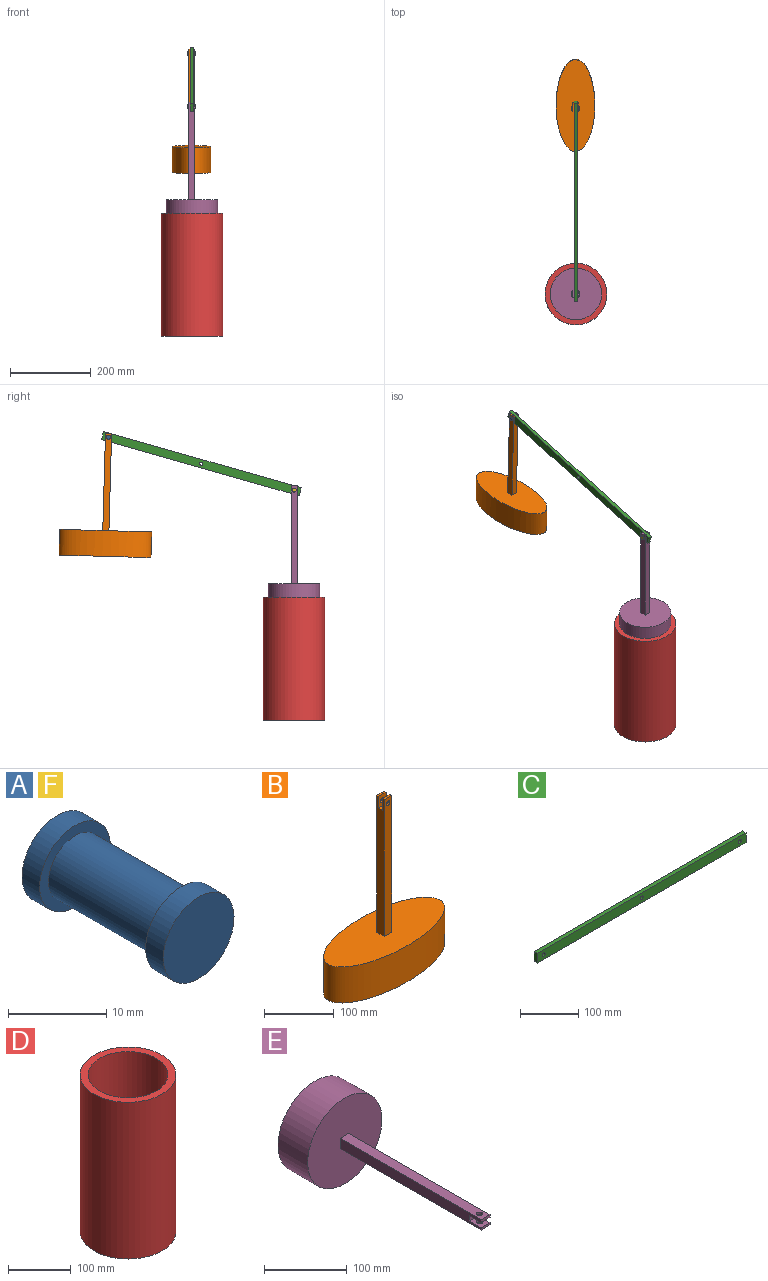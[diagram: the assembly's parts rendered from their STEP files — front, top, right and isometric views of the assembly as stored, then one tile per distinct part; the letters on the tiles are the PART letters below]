
ASSEMBLY  parts=6 mates=5
PART A: 7 faces, bbox 10.2x20.3x10.2 mm
  f0: cylinder r=3.81mm len=15.24mm, axis (0,1,0), area 364.8mm2, adj f3,f6
  f1: cylinder r=5.08mm len=10.16mm, axis (0,1,0), area 81.1mm2, adj f2,f3
  f2: plane 10.16x10.16mm, normal (0,-1,0), area 81.1mm2, adj f1
  f3: plane 10.16x10.16mm, normal (0,1,0), area 35.5mm2, adj f0,f1
  f4: cylinder r=5.08mm len=10.16mm, axis (0,-1,0), area 81.1mm2, adj f5,f6
  f5: plane 10.16x10.16mm, normal (0,1,0), area 81.1mm2, adj f4
  f6: plane 10.16x10.16mm, normal (0,-1,0), area 35.5mm2, adj f0,f4
PART B: 14 faces, bbox 226.9x95.8x304.8 mm
  f0: plane 15.24x3.8mm, normal (0,0,1), area 57.9mm2, adj f4,f5,f7,f10
  f1: plane 226.88x95.83mm, normal (0,0,1), area 16843.5mm2, adj f2,f4,f5,f6,f7
  f2: extruded ~226.88x95.83mm, area 33533.4mm2, adj f1,f3
  f3: plane 226.88x95.83mm, normal (0,0,-1), area 17075.7mm2, adj f2
  f4: plane 241.3x15.24mm, normal (0,1,0), area 3631.8mm2, adj f0,f1,f5,f7,f12
  f5: plane 241.3x15.24mm, normal (-1,0,0), area 3513.6mm2, adj f0,f1,f4,f6,f8,f9,f10,f11
  f6: plane 241.3x15.24mm, normal (0,-1,0), area 3631.8mm2, adj f1,f5,f7,f8,f13
  f7: plane 241.3x15.24mm, normal (1,0,0), area 3513.6mm2, adj f0,f1,f4,f6,f8,f9,f10,f11
  f8: plane 15.24x3.38mm, normal (0,0,1), area 51.5mm2, adj f5,f6,f7,f9
  f9: plane 20.32x15.24mm, normal (0,1,0), area 264.1mm2, adj f5,f7,f8,f11,f13
  f10: plane 20.32x15.24mm, normal (0,-1,0), area 264.1mm2, adj f0,f5,f7,f11,f12
  f11: plane 15.24x8.06mm, normal (0,0,1), area 122.8mm2, adj f5,f7,f9,f10
  f12: cylinder r=3.81mm len=7.62mm, axis (0,-1,0), area 90.9mm2, adj f4,f10
  f13: cylinder r=3.81mm len=7.62mm, axis (0,1,0), area 81mm2, adj f6,f9
PART C: 9 faces, bbox 508x8.1x20.3 mm
  f0: plane 20.32x8.05mm, normal (1,0,0), area 163.6mm2, adj f1,f3,f4,f5
  f1: plane 508x8.05mm, normal (0,0,1), area 4090.3mm2, adj f0,f2,f4,f5
  f2: plane 20.32x8.05mm, normal (-1,0,0), area 163.6mm2, adj f1,f3,f4,f5
  f3: plane 508x8.05mm, normal (0,0,-1), area 4090.3mm2, adj f0,f2,f4,f5
  f4: plane 508x20.32mm, normal (0,-1,0), area 10185.7mm2, adj f0,f1,f2,f3,f6,f7,f8
  f5: plane 508x20.32mm, normal (0,1,0), area 10185.7mm2, adj f0,f1,f2,f3,f6,f7,f8
  f6: cylinder r=3.81mm len=8.05mm, axis (0,-1,0), area 192.8mm2, adj f4,f5
  f7: cylinder r=3.81mm len=8.05mm, axis (0,-1,0), area 192.8mm2, adj f4,f5
  f8: cylinder r=3.81mm len=8.05mm, axis (0,-1,0), area 192.8mm2, adj f4,f5
PART D: 4 faces, bbox 152.4x152.4x304.8 mm
  f0: cylinder r=76.2mm len=304.8mm, axis (0,0,-1), area 145931.8mm2, adj f1,f2
  f1: plane 152.4x152.4mm, normal (0,0,1), area 5573.8mm2, adj f0,f3
  f2: plane 152.4x152.4mm, normal (0,0,-1), area 5573.8mm2, adj f0,f3
  f3: cylinder r=63.5mm len=304.8mm, axis (0,0,-1), area 121609.8mm2, adj f1,f2
PART E: 14 faces, bbox 127x292.1x127 mm
  f0: plane 15.24x3.33mm, normal (0,-1,0), area 50.7mm2, adj f1,f6,f7,f11
  f1: plane 241.3x15.24mm, normal (-1,0,0), area 3513.8mm2, adj f0,f2,f5,f6,f8,f9,f10,f11
  f2: plane 127x127mm, normal (0,-1,0), area 12435.4mm2, adj f1,f3,f5,f6,f7
  f3: cylinder r=63.5mm len=127mm, axis (0,1,0), area 20268.3mm2, adj f2,f4
  f4: plane 127x127mm, normal (0,1,0), area 12667.7mm2, adj f3
  f5: plane 241.3x15.24mm, normal (0,0,1), area 3631.8mm2, adj f1,f2,f7,f8,f12
  f6: plane 241.3x15.24mm, normal (0,0,-1), area 3631.8mm2, adj f0,f1,f2,f7,f13
  f7: plane 241.3x15.24mm, normal (1,0,0), area 3513.8mm2, adj f0,f2,f5,f6,f8,f9,f10,f11
  f8: plane 15.24x3.86mm, normal (0,-1,0), area 58.8mm2, adj f1,f5,f7,f9
  f9: plane 20.32x15.24mm, normal (0,0,-1), area 264.1mm2, adj f1,f7,f8,f10,f12
  f10: plane 15.24x8.05mm, normal (0,-1,0), area 122.7mm2, adj f1,f7,f9,f11
  f11: plane 20.32x15.24mm, normal (0,0,1), area 264.1mm2, adj f0,f1,f7,f10,f13
  f12: cylinder r=3.81mm len=7.62mm, axis (0,0,-1), area 92.4mm2, adj f5,f9
  f13: cylinder r=3.81mm len=7.62mm, axis (0,0,1), area 79.7mm2, adj f6,f11
PART F: same geometry as A
PLACE A rot(axis=(0.14,-0.14,0.98),91.1deg) t=(-7.9,853.03,569.64)mm
PLACE B rot(axis=(0.01,-0.01,1),90deg) t=(-1.17,241.29,399.26)mm
PLACE C rot(axis=(0.14,0.14,-0.98),91.1deg) t=(3.75,-362.04,237.35)mm
PLACE D at identity
PLACE E rot(axis=(-0.58,-0.58,0.58),120deg) t=(-109.54,216.91,287.46)mm
PLACE F rot(axis=(0,0,-1),90deg) t=(7.34,-344.18,336.02)mm
MATE fastened F.f0 <-> E.f12  axis (-1,0,0) through (7.34,-0.58,569.4)mm
MATE fastened A.f0 <-> C.f6  axis (-1,0,0) through (-0.28,458.67,700.08)mm
MATE slider E.f3 <-> D.f3  axis (0,0,-1) through (0,0,287.46)mm
MATE revolute B.f12 <-> C.f6  axis (1,0,0) through (-4.3,458.67,700.08)mm
MATE revolute C.f7 <-> F.f0  axis (-1,0,0) through (-0.28,-0.58,569.4)mm
